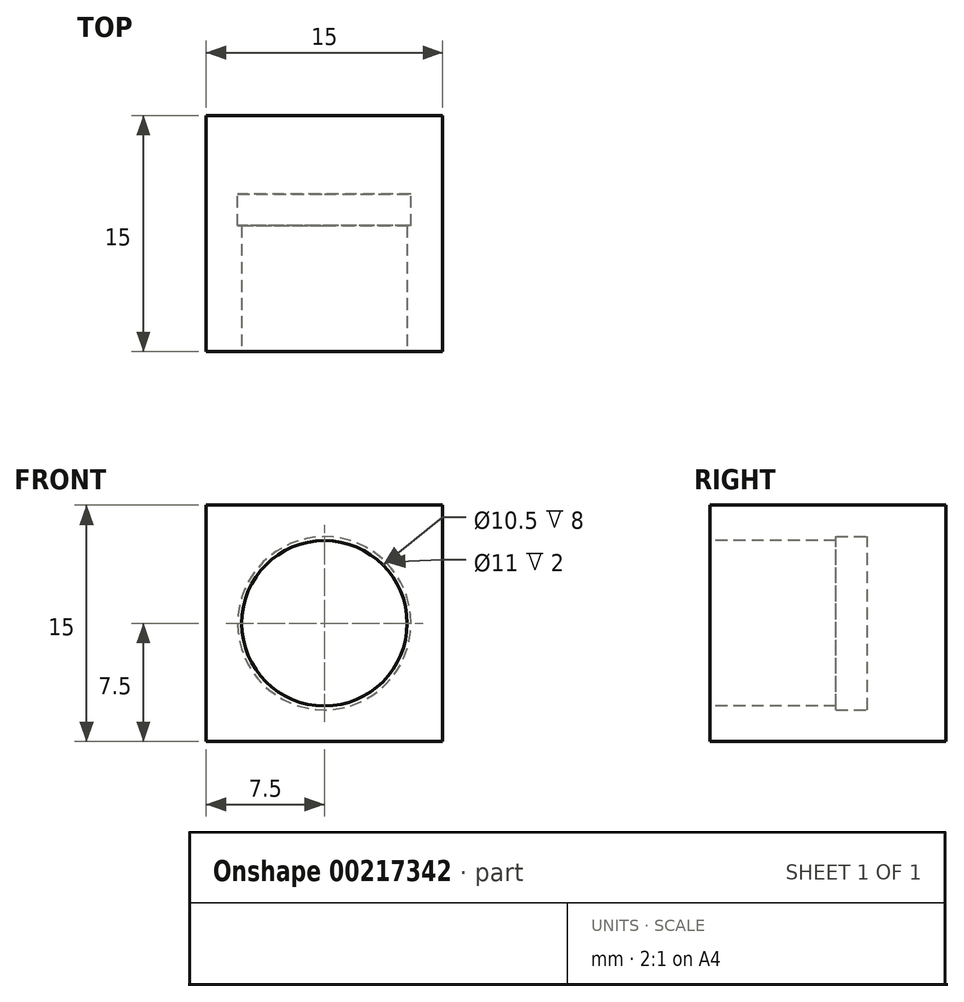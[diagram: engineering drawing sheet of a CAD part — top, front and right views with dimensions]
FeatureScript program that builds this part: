
annotation { "Feature Type Name" : "Feature", "Feature Type Description" : "" }
export const myFeature = defineFeature(function(context is Context, id is Id, definition is map)
    precondition{}
    {
        {
            var Q0;
            Q0=qCreatedBy(makeId("Front.planeOp"),FACE);
            var sketch = newSketch(context, id + "F0", { "sketchPlane" : qUnion([Q0])});
            skLineSegment(sketch, "E0.bottom", {"start": v(7.5, 7.5) * mm, "end": v(-7.5, 7.5) * mm});
            skLineSegment(sketch, "E0.top", {"start": v(7.5, -7.5) * mm, "end": v(-7.5, -7.5) * mm});
            skLineSegment(sketch, "E0.left", {"start": v(7.5, 7.5) * mm, "end": v(7.5, -7.5) * mm});
            skLineSegment(sketch, "E0.right", {"start": v(-7.5, 7.5) * mm, "end": v(-7.5, -7.5) * mm});
            skPoint(sketch, "E0.middle", {"position": v(0, 0) * mm});
            skSolve(sketch);
        }
        {
            var Q0;
            Q0=makeQuery(id+"F0.imprint","IMPRINT",FACE,{"disambiguationData":[TD([[makeQuery(id+"F0.imprint","IMPRINT",EDGE,{"derivedFrom":sQuery(id+"F0.wireOp",EDGE,"E0.bottom")}),1.0]])]});
            extrude(context, id + "F1", {"entities" : qUnion([Q0]), "depth" : 15 * mm});
        }
        {
            var Q0;
            Q0=makeQuery(id+"F1.opExtrude","CAP_FACE",FACE,{"disambiguationData":[OSD([sQuery(id+"F0.wireOp",EDGE,"E0.bottom"),sQuery(id+"F0.wireOp",EDGE,"E0.top"),sQuery(id+"F0.wireOp",EDGE,"E0.left"),sQuery(id+"F0.wireOp",EDGE,"E0.right")])],"isStart":false});
            var sketch = newSketch(context, id + "F2", { "sketchPlane" : qUnion([Q0])});
            skCircle(sketch, "E1", {"center": v(0, 0) * mm, "radius": 5.25 * mm});
            skSolve(sketch);
        }
        {
            var Q0;
            Q0=makeQuery(id+"F2.imprint","IMPRINT",FACE,{"disambiguationData":[TD([[makeQuery(id+"F2.imprint","IMPRINT",EDGE,{"derivedFrom":sQuery(id+"F2.wireOp",EDGE,"E1")}),1.0]])]});
            extrude(context, id + "F3", {"entities" : qUnion([Q0]), "operationType" : NewBodyOperationType.REMOVE, "oppositeDirection" : true, "depth" : 10 * mm});
        }
        {
            var Q0;
            Q0=makeQuery(id+"F3.boolean.opBoolean","COPY",FACE,{"derivedFrom":makeQuery(id+"F3.opExtrude","CAP_FACE",FACE,{"disambiguationData":[OSD([sQuery(id+"F2.wireOp",EDGE,"E1")])],"isStart":false})});
            var sketch = newSketch(context, id + "F4", { "sketchPlane" : qUnion([Q0])});
            skCircle(sketch, "E2", {"center": v(0, 0) * mm, "radius": 5.5 * mm});
            skSolve(sketch);
        }
        {
            var Q0;
            Q0=makeQuery(id+"F4.imprint","IMPRINT",FACE,{"disambiguationData":[TD([[makeQuery(id+"F4.imprint","IMPRINT",EDGE,{"derivedFrom":sQuery(id+"F4.wireOp",EDGE,"E2")}),1.0]])]});
            extrude(context, id + "F5", {"entities" : qUnion([Q0]), "operationType" : NewBodyOperationType.REMOVE, "depth" : 2 * mm});
        }
    });
